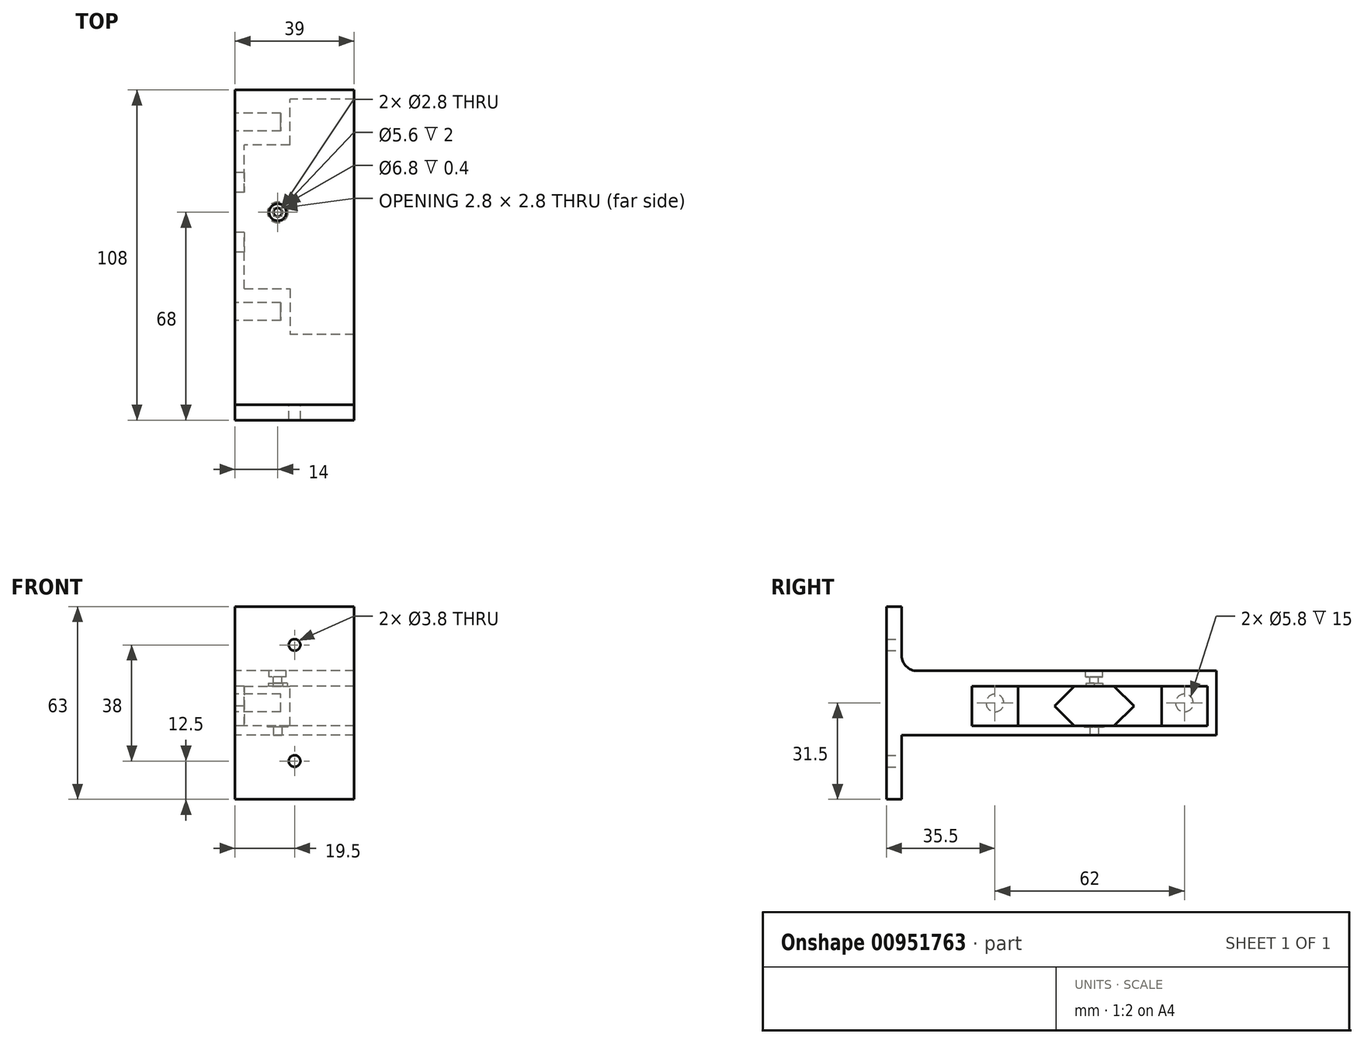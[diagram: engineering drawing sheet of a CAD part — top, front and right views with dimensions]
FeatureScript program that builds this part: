
annotation { "Feature Type Name" : "Feature", "Feature Type Description" : "" }
export const myFeature = defineFeature(function(context is Context, id is Id, definition is map)
    precondition{}
    {
        {
            var Q0;
            Q0=qCreatedBy(makeId("Top.planeOp"),FACE);
            var sketch = newSketch(context, id + "F0", { "sketchPlane" : qUnion([Q0])});
            skLineSegment(sketch, "E0", {"start": v(0, 83) * mm, "end": v(0, 0) * mm});
            skLineSegment(sketch, "E1", {"start": v(0, 0) * mm, "end": v(-39, 0) * mm});
            skLineSegment(sketch, "E2", {"start": v(-39, 0) * mm, "end": v(-39, 3) * mm});
            skLineSegment(sketch, "E3", {"start": v(-39, 3) * mm, "end": v(-3, 3) * mm});
            skLineSegment(sketch, "E4", {"start": v(-3, 3) * mm, "end": v(-3, 83) * mm});
            skLineSegment(sketch, "E5", {"start": v(-3, 83) * mm, "end": v(0, 83) * mm});
            skSolve(sketch);
        }
        {
            var Q0;
            Q0=qSketchRegion(id+"F0",true);
            extrude(context, id + "F1", {"entities" : qUnion([Q0]), "endBound" : BoundingType.SYMMETRIC, "depth" : 18 * mm, "offsetDistance" : 25 * mm});
        }
        {
            var Q0;
            Q0=makeQuery(id+"F1.opExtrude","CAP_FACE",FACE,{"disambiguationData":[OSD([sQuery(id+"F0.wireOp",EDGE,"E0"),sQuery(id+"F0.wireOp",EDGE,"E1"),sQuery(id+"F0.wireOp",EDGE,"E2"),sQuery(id+"F0.wireOp",EDGE,"E3"),sQuery(id+"F0.wireOp",EDGE,"E4"),sQuery(id+"F0.wireOp",EDGE,"E5")])],"isStart":false});
            var sketch = newSketch(context, id + "F2", { "sketchPlane" : qUnion([Q0])});
            skLineSegment(sketch, "E6.0", {"start": v(0, 83) * mm, "end": v(0, 0) * mm});
            skLineSegment(sketch, "E6.1", {"start": v(0, 0) * mm, "end": v(-39, 0) * mm});
            skLineSegment(sketch, "E7", {"start": v(-39, 0) * mm, "end": v(-39, 83) * mm});
            skLineSegment(sketch, "E8", {"start": v(-39, 83) * mm, "end": v(0, 83) * mm});
            skSolve(sketch);
        }
        {
            var Q0;
            Q0=qSketchRegion(id+"F2",true);
            extrude(context, id + "F3", {"entities" : qUnion([Q0]), "operationType" : NewBodyOperationType.ADD, "oppositeDirection" : true, "depth" : 5 * mm, "offsetDistance" : 25 * mm});
        }
        {
            var Q0;
            Q0=makeQuery(id+"F3.boolean.opBoolean","MERGE",FACE,{"derivedFrom":[makeQuery(id+"F1.opExtrude","CAP_FACE",FACE,{"disambiguationData":[OSD([sQuery(id+"F0.wireOp",EDGE,"E0"),sQuery(id+"F0.wireOp",EDGE,"E1"),sQuery(id+"F0.wireOp",EDGE,"E2"),sQuery(id+"F0.wireOp",EDGE,"E3"),sQuery(id+"F0.wireOp",EDGE,"E4"),sQuery(id+"F0.wireOp",EDGE,"E5")])],"isStart":false}),makeQuery(id+"F3.opExtrude","CAP_FACE",FACE,{"disambiguationData":[OSD([sQuery(id+"F2.wireOp",EDGE,"E6.0"),sQuery(id+"F2.wireOp",EDGE,"E6.1"),sQuery(id+"F2.wireOp",EDGE,"E7"),sQuery(id+"F2.wireOp",EDGE,"E8")])],"isStart":true})]});
            var sketch = newSketch(context, id + "F4", { "sketchPlane" : qUnion([Q0])});
            skCircle(sketch, "E9", {"center": v(-22, 60.5) * mm, "radius": 1.9 * mm});
            skCircle(sketch, "E10", {"center": v(-22, 25.5) * mm, "radius": 1.9 * mm});
            skLineSegment(sketch, "E11", {"start": v(-22, 60.5) * mm, "end": v(-22, 83) * mm});
            skLineSegment(sketch, "E12", {"start": v(-22, 25.5) * mm, "end": v(-22, 3) * mm});
            skSolve(sketch);
        }
        {
            var Q0;
            Q0=makeQuery(id+"F3.boolean.opBoolean","MERGE",FACE,{"derivedFrom":[makeQuery(id+"F1.opExtrude","SWEPT_FACE",FACE,{"disambiguationData":[OSD([sQuery(id+"F0.wireOp",EDGE,"E5")])]}),makeQuery(id+"F3.opExtrude","SWEPT_FACE",FACE,{"disambiguationData":[OSD([sQuery(id+"F2.wireOp",EDGE,"E8")])]})]});
            var sketch = newSketch(context, id + "F5", { "sketchPlane" : qUnion([Q0])});
            skLineSegment(sketch, "E13", {"start": v(0, 9) * mm, "end": v(18, 9) * mm});
            skLineSegment(sketch, "E14", {"start": v(18, 9) * mm, "end": v(18, -9) * mm});
            skLineSegment(sketch, "E15", {"start": v(18, -9) * mm, "end": v(0, -9) * mm});
            skLineSegment(sketch, "E16", {"start": v(0, -9) * mm, "end": v(0, 9) * mm});
            skSolve(sketch);
        }
        {
            var Q0;
            {var subQ5=makeQuery(id+"F1.opExtrude","SWEPT_EDGE",EDGE,{"disambiguationData":[OSD([sQuery(id+"F0.wireOp",EDGE,"E4"),sQuery(id+"F0.wireOp",EDGE,"E5")])]});Q0=makeQuery(id+"F5.imprint","IMPRINT",FACE,{"disambiguationData":[TD([[makeQuery(id+"F5.imprint","IMPRINT",EDGE,{"derivedFrom":subQ5}),1.0]])]});}
            extrude(context, id + "F6", {"entities" : qUnion([Q0]), "operationType" : NewBodyOperationType.ADD, "oppositeDirection" : true, "depth" : 18 * mm, "offsetDistance" : 25 * mm});
        }
        {
            var Q0;
            Q0=makeQuery(id+"F6.boolean.opBoolean","MERGE",FACE,{"derivedFrom":[makeQuery(id+"F1.opExtrude","CAP_FACE",FACE,{"disambiguationData":[OSD([sQuery(id+"F0.wireOp",EDGE,"E0"),sQuery(id+"F0.wireOp",EDGE,"E1"),sQuery(id+"F0.wireOp",EDGE,"E2"),sQuery(id+"F0.wireOp",EDGE,"E3"),sQuery(id+"F0.wireOp",EDGE,"E4"),sQuery(id+"F0.wireOp",EDGE,"E5")])],"isStart":true}),makeQuery(id+"F6.opExtrude","SWEPT_FACE",FACE,{"disambiguationData":[OSD([sQuery(id+"F5.wireOp",EDGE,"E15")])]})]});
            var sketch = newSketch(context, id + "F7", { "sketchPlane" : qUnion([Q0])});
            skLineSegment(sketch, "E17", {"start": v(0, 0) * mm, "end": v(-18, 0) * mm});
            skLineSegment(sketch, "E18", {"start": v(-18, 0) * mm, "end": v(-18, -18) * mm});
            skLineSegment(sketch, "E19", {"start": v(-18, -18) * mm, "end": v(0, -18) * mm});
            skLineSegment(sketch, "E20", {"start": v(0, -18) * mm, "end": v(0, 0) * mm});
            skSolve(sketch);
        }
        {
            var Q0;
            Q0=qSketchRegion(id+"F7",true);
            extrude(context, id + "F8", {"entities" : qUnion([Q0]), "operationType" : NewBodyOperationType.ADD, "oppositeDirection" : true, "depth" : 18 * mm, "offsetDistance" : 25 * mm});
        }
        {
            var Q0;
            Q0=makeQuery(id+"F8.boolean.opBoolean","MERGE",FACE,{"derivedFrom":[makeQuery(id+"F6.boolean.opBoolean","MERGE",FACE,{"derivedFrom":[makeQuery(id+"F1.opExtrude","CAP_FACE",FACE,{"disambiguationData":[OSD([sQuery(id+"F0.wireOp",EDGE,"E0"),sQuery(id+"F0.wireOp",EDGE,"E1"),sQuery(id+"F0.wireOp",EDGE,"E2"),sQuery(id+"F0.wireOp",EDGE,"E3"),sQuery(id+"F0.wireOp",EDGE,"E4"),sQuery(id+"F0.wireOp",EDGE,"E5")])],"isStart":true}),makeQuery(id+"F6.opExtrude","SWEPT_FACE",FACE,{"disambiguationData":[OSD([sQuery(id+"F5.wireOp",EDGE,"E15")])]})]}),makeQuery(id+"F8.opExtrude","CAP_FACE",FACE,{"disambiguationData":[OSD([sQuery(id+"F7.wireOp",EDGE,"E17"),sQuery(id+"F7.wireOp",EDGE,"E18"),sQuery(id+"F7.wireOp",EDGE,"E19"),sQuery(id+"F7.wireOp",EDGE,"E20")])],"isStart":true})]});
            var sketch = newSketch(context, id + "F9", { "sketchPlane" : qUnion([Q0])});
            skLineSegment(sketch, "E21.0.0", {"start": v(0, -83) * mm, "end": v(-22, -83) * mm});
            skLineSegment(sketch, "E21.0.1", {"start": v(-22, -83) * mm, "end": v(-39, -83) * mm});
            skLineSegment(sketch, "E21.0.2", {"start": v(-39, -83) * mm, "end": v(-39, 0) * mm});
            skLineSegment(sketch, "E21.0.3", {"start": v(-39, 0) * mm, "end": v(0, 0) * mm});
            skLineSegment(sketch, "E21.0.4", {"start": v(0, 0) * mm, "end": v(0, -83) * mm});
            skSolve(sketch);
        }
        {
            var Q0;
            Q0=qSketchRegion(id+"F9",true);
            extrude(context, id + "F10", {"entities" : qUnion([Q0]), "operationType" : NewBodyOperationType.ADD, "depth" : 3 * mm, "offsetDistance" : 25 * mm});
        }
        {
            var Q0;
            Q0=makeQuery(id+"F4.imprint","IMPRINT",FACE,{"disambiguationData":[TD([[makeQuery(id+"F4.imprint","IMPRINT",EDGE,{"derivedFrom":sQuery(id+"F4.wireOp",EDGE,"E9")}),-1.0]])]});
            var sketch = newSketch(context, id + "F11", { "sketchPlane" : qUnion([Q0])});
            skCircle(sketch, "E22", {"center": v(-14, 43) * mm, "radius": 17.34 * mm});
            skCircle(sketch, "E23", {"center": v(-14, 43) * mm, "radius": 14.84 * mm});
            skSolve(sketch);
        }
        {
            var Q0;
            Q0=makeQuery(id+"F10.boolean.opBoolean","MERGE",FACE,{"derivedFrom":[makeQuery(id+"F1.opExtrude","SWEPT_FACE",FACE,{"disambiguationData":[OSD([sQuery(id+"F0.wireOp",EDGE,"E0")])]}),makeQuery(id+"F10.opExtrude","SWEPT_FACE",FACE,{"disambiguationData":[OSD([sQuery(id+"F9.wireOp",EDGE,"E21.0.4")])]})]});
            var sketch = newSketch(context, id + "F12", { "sketchPlane" : qUnion([Q0])});
            skLineSegment(sketch, "E24.top", {"start": v(36.5, -9) * mm, "end": v(49.5, -9) * mm});
            skLineSegment(sketch, "E24.left", {"start": v(36.5, 4) * mm, "end": v(36.5, -9) * mm});
            skLineSegment(sketch, "E24.right", {"start": v(49.5, 4) * mm, "end": v(49.5, -9) * mm});
            skLineSegment(sketch, "E25", {"start": v(36.5, 4) * mm, "end": v(30, -2.5) * mm});
            skPoint(sketch, "E25.endSnap0", {"position": v(36.5, -2.5) * mm});
            skLineSegment(sketch, "E26", {"start": v(30, -2.5) * mm, "end": v(36.5, -9) * mm});
            skLineSegment(sketch, "E27", {"start": v(49.5, 4) * mm, "end": v(56, -2.5) * mm});
            skLineSegment(sketch, "E28", {"start": v(56, -2.5) * mm, "end": v(49.5, -9) * mm});
            skCircle(sketch, "E29", {"center": v(10.5, -1.5) * mm, "radius": 2.9 * mm});
            skCircle(sketch, "E30", {"center": v(72.5, -1.5) * mm, "radius": 2.9 * mm});
            skLineSegment(sketch, "E31", {"start": v(0, -1.5) * mm, "end": v(10.5, -1.5) * mm});
            skLineSegment(sketch, "E32", {"start": v(72.5, -1.5) * mm, "end": v(83, -1.5) * mm});
            skLineSegment(sketch, "E33", {"start": v(10.5, -1.5) * mm, "end": v(10.5, -12) * mm});
            skLineSegment(sketch, "E34", {"start": v(49.5, 4) * mm, "end": v(36.5, 4) * mm});
            skSolve(sketch);
        }
        {
            var Q0;
            {var subQ0=sQuery(id+"F12.wireOp",EDGE,"E31");var subQ1=sQuery(id+"F12.wireOp",EDGE,"E29");var subQ2=makeQuery(id+"F12.imprint","INTERSECT",VERTEX,{"derivedFrom":[subQ1,subQ0]});Q0=makeQuery(id+"F12.imprint","IMPRINT",FACE,{"disambiguationData":[TD([[makeQuery(id+"F12.imprint","IMPRINT",EDGE,{"disambiguationData":[TD([[subQ2,-1.0]])],"derivedFrom":subQ1}),1.0]])]});}
            var Q1;
            {var subQ0=sQuery(id+"F12.wireOp",EDGE,"E31");var subQ1=sQuery(id+"F12.wireOp",EDGE,"E29");var subQ2=makeQuery(id+"F12.imprint","INTERSECT",VERTEX,{"derivedFrom":[subQ1,subQ0]});Q1=makeQuery(id+"F12.imprint","IMPRINT",FACE,{"disambiguationData":[TD([[makeQuery(id+"F12.imprint","IMPRINT",EDGE,{"disambiguationData":[TD([[subQ2,1.0]])],"derivedFrom":subQ1}),1.0]])]});}
            var Q2;
            Q2=makeQuery(id+"F12.imprint","IMPRINT",FACE,{"disambiguationData":[TD([[makeQuery(id+"F12.imprint","IMPRINT",EDGE,{"derivedFrom":sQuery(id+"F12.wireOp",EDGE,"E24.left")}),-1.0]])]});
            var Q3;
            Q3=makeQuery(id+"F12.imprint","IMPRINT",FACE,{"disambiguationData":[TD([[makeQuery(id+"F12.imprint","IMPRINT",EDGE,{"derivedFrom":sQuery(id+"F12.wireOp",EDGE,"E24.top")}),1.0]])]});
            var Q4;
            Q4=makeQuery(id+"F12.imprint","IMPRINT",FACE,{"disambiguationData":[TD([[makeQuery(id+"F12.imprint","IMPRINT",EDGE,{"derivedFrom":sQuery(id+"F12.wireOp",EDGE,"E24.right")}),1.0]])]});
            var Q5;
            Q5=makeQuery(id+"F12.imprint","IMPRINT",FACE,{"disambiguationData":[TD([[makeQuery(id+"F12.imprint","IMPRINT",EDGE,{"derivedFrom":sQuery(id+"F12.wireOp",EDGE,"E30")}),1.0]])]});
            extrude(context, id + "F13", {"entities" : qUnion([Q0, Q1, Q2, Q3, Q4, Q5]), "operationType" : NewBodyOperationType.REMOVE, "oppositeDirection" : true, "depth" : 15 * mm, "offsetDistance" : 25 * mm});
        }
        {
            var Q0;
            Q0=makeQuery(id+"F6.opExtrude","SWEPT_FACE",FACE,{"disambiguationData":[OSD([sQuery(id+"F5.wireOp",EDGE,"E14")])]});
            var sketch = newSketch(context, id + "F14", { "sketchPlane" : qUnion([Q0])});
            skLineSegment(sketch, "E35", {"start": v(-83, 4) * mm, "end": v(-80, 4) * mm});
            skLineSegment(sketch, "E36", {"start": v(-80, 4) * mm, "end": v(-80, -9) * mm});
            skLineSegment(sketch, "E37", {"start": v(-80, -9) * mm, "end": v(-83, -9) * mm});
            skLineSegment(sketch, "E38", {"start": v(-83, -9) * mm, "end": v(-83, 4) * mm});
            skSolve(sketch);
        }
        {
            var Q0;
            Q0=makeQuery(id+"F14.imprint","IMPRINT",FACE,{"disambiguationData":[TD([[makeQuery(id+"F14.imprint","IMPRINT",EDGE,{"derivedFrom":sQuery(id+"F14.wireOp",EDGE,"E35")}),1.0]])]});
            var Q1;
            Q1=makeQuery(id+"F10.boolean.opBoolean","MERGE",FACE,{"derivedFrom":[makeQuery(id+"F3.boolean.opBoolean","MERGE",FACE,{"derivedFrom":[makeQuery(id+"F1.opExtrude","SWEPT_FACE",FACE,{"disambiguationData":[OSD([sQuery(id+"F0.wireOp",EDGE,"E2")])]}),makeQuery(id+"F3.opExtrude","SWEPT_FACE",FACE,{"disambiguationData":[OSD([sQuery(id+"F2.wireOp",EDGE,"E7")])]})]}),makeQuery(id+"F10.opExtrude","SWEPT_FACE",FACE,{"disambiguationData":[OSD([sQuery(id+"F9.wireOp",EDGE,"E21.0.2")])]})]});
            extrude(context, id + "F15", {"entities" : qUnion([Q0]), "operationType" : NewBodyOperationType.ADD, "endBound" : BoundingType.UP_TO_SURFACE, "depth" : 25 * mm, "endBoundEntityFace" : qUnion([Q1]), "offsetDistance" : 25 * mm});
        }
        {
            var Q0;
            Q0=makeQuery(id+"F10.boolean.opBoolean","MERGE",FACE,{"derivedFrom":[makeQuery(id+"F1.opExtrude","SWEPT_FACE",FACE,{"disambiguationData":[OSD([sQuery(id+"F0.wireOp",EDGE,"E1")])]}),makeQuery(id+"F10.opExtrude","SWEPT_FACE",FACE,{"disambiguationData":[OSD([sQuery(id+"F9.wireOp",EDGE,"E21.0.3")])]})]});
            var sketch = newSketch(context, id + "F16", { "sketchPlane" : qUnion([Q0])});
            skLineSegment(sketch, "E39.0", {"start": v(0, -12) * mm, "end": v(-39, -12) * mm});
            skLineSegment(sketch, "E39.1", {"start": v(0, 9) * mm, "end": v(0, -12) * mm});
            skLineSegment(sketch, "E39.2", {"start": v(0, 9) * mm, "end": v(-39, 9) * mm});
            skLineSegment(sketch, "E39.3", {"start": v(-39, 9) * mm, "end": v(-39, -12) * mm});
            skSolve(sketch);
        }
        {
            var Q0;
            Q0=makeQuery(id+"F16.imprint","IMPRINT",FACE,{"disambiguationData":[TD([[makeQuery(id+"F16.imprint","IMPRINT",EDGE,{"derivedFrom":sQuery(id+"F16.wireOp",EDGE,"E39.0")}),-1.0]])]});
            extrude(context, id + "F17", {"entities" : qUnion([Q0]), "operationType" : NewBodyOperationType.ADD, "depth" : 20 * mm, "offsetDistance" : 25 * mm});
        }
        {
            var Q0;
            Q0=makeQuery(id+"F17.opExtrude","CAP_FACE",FACE,{"disambiguationData":[OSD([sQuery(id+"F16.wireOp",EDGE,"E39.0"),sQuery(id+"F16.wireOp",EDGE,"E39.1"),sQuery(id+"F16.wireOp",EDGE,"E39.2"),sQuery(id+"F16.wireOp",EDGE,"E39.3")])],"isStart":false});
            var sketch = newSketch(context, id + "F18", { "sketchPlane" : qUnion([Q0])});
            skLineSegment(sketch, "E40", {"start": v(-39, 30) * mm, "end": v(-39, 9) * mm});
            skLineSegment(sketch, "E41", {"start": v(-39, 9) * mm, "end": v(-39, -12) * mm});
            skLineSegment(sketch, "E42", {"start": v(-39, -12) * mm, "end": v(-39, -33) * mm});
            skLineSegment(sketch, "E43", {"start": v(-39, -33) * mm, "end": v(0, -33) * mm});
            skLineSegment(sketch, "E44", {"start": v(0, -33) * mm, "end": v(0, -12) * mm});
            skLineSegment(sketch, "E45", {"start": v(0, -12) * mm, "end": v(0, 9) * mm});
            skLineSegment(sketch, "E46", {"start": v(0, 9) * mm, "end": v(0, 30) * mm});
            skLineSegment(sketch, "E47", {"start": v(0, 30) * mm, "end": v(-39, 30) * mm});
            skSolve(sketch);
        }
        {
            var Q0;
            Q0=qSketchRegion(id+"F18",true);
            extrude(context, id + "F19", {"entities" : qUnion([Q0]), "operationType" : NewBodyOperationType.ADD, "depth" : 3 * mm, "offsetDistance" : 25 * mm});
        }
        {
            var Q0;
            Q0=makeQuery(id+"F17.opExtrude","CAP_EDGE",EDGE,{"disambiguationData":[OSD([sQuery(id+"F16.wireOp",EDGE,"E39.0")])],"isStart":false});
            var Q1;
            Q1=makeQuery(id+"F17.opExtrude","CAP_EDGE",EDGE,{"disambiguationData":[OSD([sQuery(id+"F16.wireOp",EDGE,"E39.2")])],"isStart":false});
            fillet(context, id + "F20", {"entities" : qUnion([Q0, Q1]), "radius" : 5 * mm, "tangentPropagation" : true, "allowEdgeOverflow" : false});
        }
        {
            var Q0;
            Q0=makeQuery(id+"F19.opExtrude","CAP_FACE",FACE,{"disambiguationData":[OSD([sQuery(id+"F18.wireOp",EDGE,"E40"),sQuery(id+"F18.wireOp",EDGE,"E41"),sQuery(id+"F18.wireOp",EDGE,"E42"),sQuery(id+"F18.wireOp",EDGE,"E43"),sQuery(id+"F18.wireOp",EDGE,"E44"),sQuery(id+"F18.wireOp",EDGE,"E45"),sQuery(id+"F18.wireOp",EDGE,"E46"),sQuery(id+"F18.wireOp",EDGE,"E47")])],"isStart":false});
            var sketch = newSketch(context, id + "F21", { "sketchPlane" : qUnion([Q0])});
            skLineSegment(sketch, "E48.bottom", {"start": v(-32, 23) * mm, "end": v(-7, 23) * mm});
            skLineSegment(sketch, "E48.top", {"start": v(-32, -26) * mm, "end": v(-7, -26) * mm});
            skLineSegment(sketch, "E48.left", {"start": v(-32, 23) * mm, "end": v(-32, -26) * mm});
            skLineSegment(sketch, "E48.right", {"start": v(-7, 23) * mm, "end": v(-7, -26) * mm});
            skCircle(sketch, "E49", {"center": v(-32, -26) * mm, "radius": 1.9 * mm});
            skCircle(sketch, "E50", {"center": v(-7, -26) * mm, "radius": 1.9 * mm});
            skCircle(sketch, "E51", {"center": v(-7, 23) * mm, "radius": 1.9 * mm});
            skCircle(sketch, "E52", {"center": v(-32, 23) * mm, "radius": 1.9 * mm});
            skSolve(sketch);
        }
        {
            var Q0;
            {var subQ0=sQuery(id+"F21.wireOp",EDGE,"E48.left");var subQ1=sQuery(id+"F21.wireOp",EDGE,"E48.bottom");var subQ2=makeQuery(id+"F21.imprint","INTERSECT",VERTEX,{"derivedFrom":[subQ1,subQ0]});Q0=makeQuery(id+"F21.imprint","IMPRINT",FACE,{"disambiguationData":[TD([[makeQuery(id+"F21.imprint","IMPRINT",EDGE,{"disambiguationData":[TD([[subQ2,-1.0]])],"derivedFrom":subQ1}),1.0]])]});}
            var Q1;
            {var subQ0=sQuery(id+"F21.wireOp",EDGE,"E48.left");var subQ1=sQuery(id+"F21.wireOp",EDGE,"E48.bottom");var subQ2=makeQuery(id+"F21.imprint","INTERSECT",VERTEX,{"derivedFrom":[subQ1,subQ0]});Q1=makeQuery(id+"F21.imprint","IMPRINT",FACE,{"disambiguationData":[TD([[makeQuery(id+"F21.imprint","IMPRINT",EDGE,{"disambiguationData":[TD([[subQ2,-1.0]])],"derivedFrom":subQ1}),-1.0]])]});}
            var Q2;
            {var subQ0=sQuery(id+"F21.wireOp",EDGE,"E48.right");var subQ1=sQuery(id+"F21.wireOp",EDGE,"E48.bottom");var subQ2=makeQuery(id+"F21.imprint","INTERSECT",VERTEX,{"derivedFrom":[subQ1,subQ0]});Q2=makeQuery(id+"F21.imprint","IMPRINT",FACE,{"disambiguationData":[TD([[makeQuery(id+"F21.imprint","IMPRINT",EDGE,{"disambiguationData":[TD([[subQ2,1.0]])],"derivedFrom":subQ1}),1.0]])]});}
            var Q3;
            {var subQ0=sQuery(id+"F21.wireOp",EDGE,"E48.right");var subQ1=sQuery(id+"F21.wireOp",EDGE,"E48.bottom");var subQ2=makeQuery(id+"F21.imprint","INTERSECT",VERTEX,{"derivedFrom":[subQ1,subQ0]});Q3=makeQuery(id+"F21.imprint","IMPRINT",FACE,{"disambiguationData":[TD([[makeQuery(id+"F21.imprint","IMPRINT",EDGE,{"disambiguationData":[TD([[subQ2,1.0]])],"derivedFrom":subQ1}),-1.0]])]});}
            var Q4;
            {var subQ0=sQuery(id+"F21.wireOp",EDGE,"E48.left");var subQ1=sQuery(id+"F21.wireOp",EDGE,"E48.top");var subQ2=makeQuery(id+"F21.imprint","INTERSECT",VERTEX,{"derivedFrom":[subQ1,subQ0]});Q4=makeQuery(id+"F21.imprint","IMPRINT",FACE,{"disambiguationData":[TD([[makeQuery(id+"F21.imprint","IMPRINT",EDGE,{"disambiguationData":[TD([[subQ2,-1.0]])],"derivedFrom":subQ1}),-1.0]])]});}
            var Q5;
            {var subQ0=sQuery(id+"F21.wireOp",EDGE,"E48.left");var subQ1=sQuery(id+"F21.wireOp",EDGE,"E48.top");var subQ2=makeQuery(id+"F21.imprint","INTERSECT",VERTEX,{"derivedFrom":[subQ1,subQ0]});Q5=makeQuery(id+"F21.imprint","IMPRINT",FACE,{"disambiguationData":[TD([[makeQuery(id+"F21.imprint","IMPRINT",EDGE,{"disambiguationData":[TD([[subQ2,-1.0]])],"derivedFrom":subQ1}),1.0]])]});}
            var Q6;
            {var subQ0=sQuery(id+"F21.wireOp",EDGE,"E48.right");var subQ1=sQuery(id+"F21.wireOp",EDGE,"E48.top");var subQ2=makeQuery(id+"F21.imprint","INTERSECT",VERTEX,{"derivedFrom":[subQ1,subQ0]});Q6=makeQuery(id+"F21.imprint","IMPRINT",FACE,{"disambiguationData":[TD([[makeQuery(id+"F21.imprint","IMPRINT",EDGE,{"disambiguationData":[TD([[subQ2,1.0]])],"derivedFrom":subQ1}),-1.0]])]});}
            var Q7;
            {var subQ0=sQuery(id+"F21.wireOp",EDGE,"E48.right");var subQ1=sQuery(id+"F21.wireOp",EDGE,"E48.top");var subQ2=makeQuery(id+"F21.imprint","INTERSECT",VERTEX,{"derivedFrom":[subQ1,subQ0]});Q7=makeQuery(id+"F21.imprint","IMPRINT",FACE,{"disambiguationData":[TD([[makeQuery(id+"F21.imprint","IMPRINT",EDGE,{"disambiguationData":[TD([[subQ2,1.0]])],"derivedFrom":subQ1}),1.0]])]});}
            extrude(context, id + "F22", {"entities" : qUnion([Q0, Q1, Q2, Q3, Q4, Q5, Q6, Q7]), "operationType" : NewBodyOperationType.REMOVE, "oppositeDirection" : true, "depth" : 25 * mm, "offsetDistance" : 25 * mm});
        }
        {
            var Q0;
            {var subQ0=sQuery(id+"F11.wireOp",EDGE,"E23");var subQ1=makeQuery(id+"F4.imprint","IMPRINT",EDGE,{"derivedFrom":makeQuery(id+"F1.opExtrude","CAP_EDGE",EDGE,{"disambiguationData":[OSD([sQuery(id+"F0.wireOp",EDGE,"E0")])],"isStart":false})});var subQ2=makeQuery(id+"F11.imprint","INTERSECT",VERTEX,{"disambiguationData":[OD(0.0)],"derivedFrom":[subQ1,subQ0]});Q0=makeQuery(id+"F11.imprint","IMPRINT",FACE,{"disambiguationData":[TD([[makeQuery(id+"F11.imprint","IMPRINT",EDGE,{"disambiguationData":[TD([[subQ2,-1.0]])],"derivedFrom":subQ0}),1.0]])]});}
            var sketch = newSketch(context, id + "F23", { "sketchPlane" : qUnion([Q0])});
            skCircle(sketch, "E53", {"center": v(-14, 43) * mm, "radius": 2.4 * mm});
            skSolve(sketch);
        }
        {
            var Q0;
            Q0=makeQuery(id+"F23.imprint","IMPRINT",FACE,{"disambiguationData":[TD([[makeQuery(id+"F23.imprint","IMPRINT",EDGE,{"derivedFrom":sQuery(id+"F23.wireOp",EDGE,"E53")}),1.0]])]});
            extrude(context, id + "F24", {"entities" : qUnion([Q0]), "operationType" : NewBodyOperationType.REMOVE, "oppositeDirection" : true, "depth" : 25 * mm, "offsetDistance" : 25 * mm});
        }
        {
            var Q0;
            {var subQ11=makeQuery(id+"F4.imprint","IMPRINT",EDGE,{"derivedFrom":makeQuery(id+"F1.opExtrude","CAP_EDGE",EDGE,{"disambiguationData":[OSD([sQuery(id+"F0.wireOp",EDGE,"E1")])],"isStart":false})});Q0=makeQuery(id+"F11.imprint","IMPRINT",FACE,{"disambiguationData":[TD([[makeQuery(id+"F11.imprint","IMPRINT",EDGE,{"derivedFrom":subQ11}),-1.0]])]});}
            var sketch = newSketch(context, id + "F25", { "sketchPlane" : qUnion([Q0])});
            skCircle(sketch, "E54.cCircle", {"center": v(-14, 43) * mm, "radius": 4.73 * mm, "construction": true});
            skLineSegment(sketch, "E54.0", {"start": v(-11.63, 47.1) * mm, "end": v(-9.27, 43) * mm});
            skLineSegment(sketch, "E54.1", {"start": v(-9.27, 43) * mm, "end": v(-11.63, 38.9) * mm});
            skLineSegment(sketch, "E54.2", {"start": v(-11.63, 38.9) * mm, "end": v(-16.37, 38.9) * mm});
            skLineSegment(sketch, "E54.3", {"start": v(-16.37, 38.9) * mm, "end": v(-18.73, 43) * mm});
            skLineSegment(sketch, "E54.4", {"start": v(-18.73, 43) * mm, "end": v(-16.37, 47.1) * mm});
            skLineSegment(sketch, "E54.5", {"start": v(-16.37, 47.1) * mm, "end": v(-11.63, 47.1) * mm});
            skSolve(sketch);
        }
        {
            var Q0;
            Q0=makeQuery(id+"F25.imprint","IMPRINT",FACE,{"disambiguationData":[TD([[makeQuery(id+"F25.imprint","IMPRINT",EDGE,{"derivedFrom":sQuery(id+"F25.wireOp",EDGE,"E54.0")}),-1.0]])]});
            extrude(context, id + "F26", {"entities" : qUnion([Q0]), "operationType" : NewBodyOperationType.REMOVE, "oppositeDirection" : true, "depth" : 2.5 * mm, "offsetDistance" : 25 * mm});
        }
        {
            var Q0;
            Q0=qCreatedBy(makeId("Right.planeOp"),FACE);
            cPlane(context, id + "F27", {"entities" : qUnion([Q0]), "cplaneType" : CPlaneType.OFFSET, "offset" : 25 * mm, "width" : 150 * mm, "height" : 150 * mm});
        }
        {
            var Q0;
            Q0=makeQuery(id+"F1.opExtrude","SWEPT_BODY",BODY,{"disambiguationData":[OSD([sQuery(id+"F0.wireOp",EDGE,"E0"),sQuery(id+"F0.wireOp",EDGE,"E1"),sQuery(id+"F0.wireOp",EDGE,"E2"),sQuery(id+"F0.wireOp",EDGE,"E3"),sQuery(id+"F0.wireOp",EDGE,"E4"),sQuery(id+"F0.wireOp",EDGE,"E5")])]});
            var Q1;
            Q1=qCreatedBy(id+"F27.planeOp",FACE);
            mirror(context, id + "F28", {"entities" : qUnion([Q0]), "mirrorPlane" : qUnion([Q1])});
        }
        {
            var Q0;
            Q0=makeQuery(id+"F28.opPattern","COPY",BODY,{"derivedFrom":makeQuery(id+"F1.opExtrude","SWEPT_BODY",BODY,{"disambiguationData":[OSD([sQuery(id+"F0.wireOp",EDGE,"E0"),sQuery(id+"F0.wireOp",EDGE,"E1"),sQuery(id+"F0.wireOp",EDGE,"E2"),sQuery(id+"F0.wireOp",EDGE,"E3"),sQuery(id+"F0.wireOp",EDGE,"E4"),sQuery(id+"F0.wireOp",EDGE,"E5")])]}),"instanceName":"1"});
            var Q1;
            Q1=qCreatedBy(id+"F27.planeOp",FACE);
            mirror(context, id + "F29", {"operationType" : NewBodyOperationType.REMOVE, "entities" : qUnion([Q0]), "mirrorPlane" : qUnion([Q1])});
        }
        {
            var Q0;
            {var subQ0=sQuery(id+"F18.wireOp",EDGE,"E46");var subQ1=sQuery(id+"F18.wireOp",EDGE,"E45");var subQ2=sQuery(id+"F18.wireOp",EDGE,"E44");var subQ6=sQuery(id+"F18.wireOp",EDGE,"E42");var subQ7=sQuery(id+"F18.wireOp",EDGE,"E41");var subQ8=sQuery(id+"F18.wireOp",EDGE,"E40");var subQ9=sQuery(id+"F18.wireOp",EDGE,"E47");Q0=makeQuery(id+"F28.opPattern","COPY",FACE,{"derivedFrom":makeQuery(id+"F19.boolean.opBoolean","SPLIT",FACE,{"disambiguationData":[TD([makeQuery(id+"F17.opExtrude","SWEPT_FACE",FACE,{"disambiguationData":[OSD([sQuery(id+"F16.wireOp",EDGE,"E39.2")])]})])],"derivedFrom":makeQuery(id+"F19.opExtrude","CAP_FACE",FACE,{"disambiguationData":[OSD([subQ8,subQ7,subQ6,sQuery(id+"F18.wireOp",EDGE,"E43"),subQ2,subQ1,subQ0,subQ9])],"isStart":true})}),"instanceName":"1"});}
            var sketch = newSketch(context, id + "F30", { "sketchPlane" : qUnion([Q0])});
            skCircle(sketch, "E55", {"center": v(-57.1, 22.38) * mm, "radius": 4.94 * mm});
            skCircle(sketch, "E56", {"center": v(-82, 23) * mm, "radius": 3.92 * mm});
            skCircle(sketch, "E57", {"center": v(-56.98, -25.74) * mm, "radius": 2.63 * mm});
            skCircle(sketch, "E58", {"center": v(-82.6, -26.07) * mm, "radius": 3.77 * mm});
            skSolve(sketch);
        }
        {
            var Q0;
            Q0 = qSketchRegion(id + "F30", true);
            var Q1;
            Q1=makeQuery(id+"F28.opPattern","COPY",FACE,{"derivedFrom":makeQuery(id+"F19.opExtrude","CAP_FACE",FACE,{"disambiguationData":[OSD([sQuery(id+"F18.wireOp",EDGE,"E40"),sQuery(id+"F18.wireOp",EDGE,"E41"),sQuery(id+"F18.wireOp",EDGE,"E42"),sQuery(id+"F18.wireOp",EDGE,"E43"),sQuery(id+"F18.wireOp",EDGE,"E44"),sQuery(id+"F18.wireOp",EDGE,"E45"),sQuery(id+"F18.wireOp",EDGE,"E46"),sQuery(id+"F18.wireOp",EDGE,"E47")])],"isStart":false}),"instanceName":"1"});
            extrude(context, id + "F31", {"entities" : qUnion([Q0]), "operationType" : NewBodyOperationType.ADD, "endBound" : BoundingType.UP_TO_SURFACE, "oppositeDirection" : true, "depth" : 25 * mm, "endBoundEntityFace" : qUnion([Q1]), "offsetDistance" : 25 * mm});
        }
        {
            var Q0;
            {var subQ0=sQuery(id+"F18.wireOp",EDGE,"E46");var subQ1=sQuery(id+"F18.wireOp",EDGE,"E45");var subQ2=sQuery(id+"F18.wireOp",EDGE,"E44");var subQ6=sQuery(id+"F18.wireOp",EDGE,"E42");var subQ7=sQuery(id+"F18.wireOp",EDGE,"E41");var subQ8=sQuery(id+"F18.wireOp",EDGE,"E40");var subQ9=sQuery(id+"F18.wireOp",EDGE,"E47");Q0=makeQuery(id+"F31.boolean.opBoolean","MERGE",FACE,{"derivedFrom":[makeQuery(id+"F28.opPattern","COPY",FACE,{"derivedFrom":makeQuery(id+"F19.boolean.opBoolean","SPLIT",FACE,{"disambiguationData":[TD([makeQuery(id+"F17.opExtrude","SWEPT_FACE",FACE,{"disambiguationData":[OSD([sQuery(id+"F16.wireOp",EDGE,"E39.2")])]})])],"derivedFrom":makeQuery(id+"F19.opExtrude","CAP_FACE",FACE,{"disambiguationData":[OSD([subQ8,subQ7,subQ6,sQuery(id+"F18.wireOp",EDGE,"E43"),subQ2,subQ1,subQ0,subQ9])],"isStart":true})}),"instanceName":"1"}),makeQuery(id+"F31.opExtrude","CAP_FACE",FACE,{"disambiguationData":[OSD([sQuery(id+"F30.wireOp",EDGE,"E55")])],"isStart":true}),makeQuery(id+"F31.opExtrude","CAP_FACE",FACE,{"disambiguationData":[OSD([sQuery(id+"F30.wireOp",EDGE,"E56")])],"isStart":true})]});}
            var sketch = newSketch(context, id + "F32", { "sketchPlane" : qUnion([Q0])});
            skCircle(sketch, "E59", {"center": v(-69.5, 17.5) * mm, "radius": 1.9 * mm});
            skCircle(sketch, "E60", {"center": v(-69.5, -20.5) * mm, "radius": 1.9 * mm});
            skLineSegment(sketch, "E61", {"start": v(-69.5, 17.5) * mm, "end": v(-69.5, -20.5) * mm});
            skLineSegment(sketch, "E62", {"start": v(-69.5, 17.5) * mm, "end": v(-69.5, 30) * mm});
            skLineSegment(sketch, "E63", {"start": v(-69.5, -20.5) * mm, "end": v(-69.5, -33) * mm});
            skSolve(sketch);
        }
        {
            var Q0;
            Q0 = qSketchRegion(id + "F32", true);
            extrude(context, id + "F33", {"entities" : qUnion([Q0]), "operationType" : NewBodyOperationType.REMOVE, "oppositeDirection" : true, "depth" : 25 * mm, "offsetDistance" : 25 * mm});
        }
        {
            var Q0;
            Q0=makeQuery(id+"F28.opPattern","COPY",FACE,{"derivedFrom":makeQuery(id+"F17.boolean.opBoolean","MERGE",FACE,{"derivedFrom":[makeQuery(id+"F3.boolean.opBoolean","MERGE",FACE,{"derivedFrom":[makeQuery(id+"F1.opExtrude","CAP_FACE",FACE,{"disambiguationData":[OSD([sQuery(id+"F0.wireOp",EDGE,"E0"),sQuery(id+"F0.wireOp",EDGE,"E1"),sQuery(id+"F0.wireOp",EDGE,"E2"),sQuery(id+"F0.wireOp",EDGE,"E3"),sQuery(id+"F0.wireOp",EDGE,"E4"),sQuery(id+"F0.wireOp",EDGE,"E5")])],"isStart":false}),makeQuery(id+"F3.opExtrude","CAP_FACE",FACE,{"disambiguationData":[OSD([sQuery(id+"F2.wireOp",EDGE,"E6.0"),sQuery(id+"F2.wireOp",EDGE,"E6.1"),sQuery(id+"F2.wireOp",EDGE,"E7"),sQuery(id+"F2.wireOp",EDGE,"E8")])],"isStart":true})]}),makeQuery(id+"F17.opExtrude","SWEPT_FACE",FACE,{"disambiguationData":[OSD([sQuery(id+"F16.wireOp",EDGE,"E39.2")])]})]}),"instanceName":"1"});
            var sketch = newSketch(context, id + "F34", { "sketchPlane" : qUnion([Q0])});
            skCircle(sketch, "E64", {"center": v(64, 43) * mm, "radius": 1.4 * mm});
            skCircle(sketch, "E65", {"center": v(64, 43) * mm, "radius": 5.83 * mm});
            skSolve(sketch);
        }
        {
            var Q0;
            Q0 = qSketchRegion(id + "F34", true);
            var Q1;
            Q1=makeQuery(id+"F28.opPattern","COPY",FACE,{"derivedFrom":makeQuery(id+"F13.boolean.opBoolean","MERGE",FACE,{"derivedFrom":[makeQuery(id+"F3.opExtrude","CAP_FACE",FACE,{"disambiguationData":[OSD([sQuery(id+"F2.wireOp",EDGE,"E6.0"),sQuery(id+"F2.wireOp",EDGE,"E6.1"),sQuery(id+"F2.wireOp",EDGE,"E7"),sQuery(id+"F2.wireOp",EDGE,"E8")])],"isStart":false})],"fromTools":[makeQuery(id+"F13.opExtrude","SWEPT_FACE",FACE,{"disambiguationData":[OSD([sQuery(id+"F12.wireOp",EDGE,"E34")])]})]}),"instanceName":"1"});
            extrude(context, id + "F35", {"entities" : qUnion([Q0]), "operationType" : NewBodyOperationType.ADD, "endBound" : BoundingType.UP_TO_SURFACE, "oppositeDirection" : true, "depth" : 25 * mm, "endBoundEntityFace" : qUnion([Q1]), "offsetDistance" : 25 * mm});
        }
        {
            var Q0;
            Q0=makeQuery(id+"F28.opPattern","COPY",FACE,{"derivedFrom":makeQuery(id+"F17.boolean.opBoolean","MERGE",FACE,{"derivedFrom":[makeQuery(id+"F10.opExtrude","CAP_FACE",FACE,{"disambiguationData":[OSD([sQuery(id+"F9.wireOp",EDGE,"E21.0.0"),sQuery(id+"F9.wireOp",EDGE,"E21.0.1"),sQuery(id+"F9.wireOp",EDGE,"E21.0.2"),sQuery(id+"F9.wireOp",EDGE,"E21.0.3"),sQuery(id+"F9.wireOp",EDGE,"E21.0.4")])],"isStart":false}),makeQuery(id+"F17.opExtrude","SWEPT_FACE",FACE,{"disambiguationData":[OSD([sQuery(id+"F16.wireOp",EDGE,"E39.0")])]})]}),"instanceName":"1"});
            var sketch = newSketch(context, id + "F36", { "sketchPlane" : qUnion([Q0])});
            skCircle(sketch, "E66", {"center": v(64, -43) * mm, "radius": 1.4 * mm});
            skCircle(sketch, "E67", {"center": v(64, -43) * mm, "radius": 4.7 * mm});
            skSolve(sketch);
        }
        {
            var Q0;
            Q0 = qSketchRegion(id + "F36", true);
            var Q1;
            Q1=makeQuery(id+"F28.opPattern","COPY",FACE,{"derivedFrom":makeQuery(id+"F13.boolean.opBoolean","MERGE",FACE,{"derivedFrom":[makeQuery(id+"F10.opExtrude","CAP_FACE",FACE,{"disambiguationData":[OSD([sQuery(id+"F9.wireOp",EDGE,"E21.0.0"),sQuery(id+"F9.wireOp",EDGE,"E21.0.1"),sQuery(id+"F9.wireOp",EDGE,"E21.0.2"),sQuery(id+"F9.wireOp",EDGE,"E21.0.3"),sQuery(id+"F9.wireOp",EDGE,"E21.0.4")])],"isStart":true})],"fromTools":[makeQuery(id+"F13.opExtrude","SWEPT_FACE",FACE,{"disambiguationData":[OSD([sQuery(id+"F12.wireOp",EDGE,"E24.top")])]})]}),"instanceName":"1"});
            extrude(context, id + "F37", {"entities" : qUnion([Q0]), "operationType" : NewBodyOperationType.ADD, "endBound" : BoundingType.UP_TO_SURFACE, "oppositeDirection" : true, "depth" : 25 * mm, "endBoundEntityFace" : qUnion([Q1]), "offsetDistance" : 25 * mm});
        }
        {
            var Q0;
            Q0=makeQuery(id+"F35.boolean.opBoolean","MERGE",FACE,{"derivedFrom":[makeQuery(id+"F28.opPattern","COPY",FACE,{"derivedFrom":makeQuery(id+"F17.boolean.opBoolean","MERGE",FACE,{"derivedFrom":[makeQuery(id+"F3.boolean.opBoolean","MERGE",FACE,{"derivedFrom":[makeQuery(id+"F1.opExtrude","CAP_FACE",FACE,{"disambiguationData":[OSD([sQuery(id+"F0.wireOp",EDGE,"E0"),sQuery(id+"F0.wireOp",EDGE,"E1"),sQuery(id+"F0.wireOp",EDGE,"E2"),sQuery(id+"F0.wireOp",EDGE,"E3"),sQuery(id+"F0.wireOp",EDGE,"E4"),sQuery(id+"F0.wireOp",EDGE,"E5")])],"isStart":false}),makeQuery(id+"F3.opExtrude","CAP_FACE",FACE,{"disambiguationData":[OSD([sQuery(id+"F2.wireOp",EDGE,"E6.0"),sQuery(id+"F2.wireOp",EDGE,"E6.1"),sQuery(id+"F2.wireOp",EDGE,"E7"),sQuery(id+"F2.wireOp",EDGE,"E8")])],"isStart":true})]}),makeQuery(id+"F17.opExtrude","SWEPT_FACE",FACE,{"disambiguationData":[OSD([sQuery(id+"F16.wireOp",EDGE,"E39.2")])]})]}),"instanceName":"1"}),makeQuery(id+"F35.opExtrude","CAP_FACE",FACE,{"disambiguationData":[OSD([sQuery(id+"F34.wireOp",EDGE,"E64"),sQuery(id+"F34.wireOp",EDGE,"E65")])],"isStart":true})]});
            var sketch = newSketch(context, id + "F38", { "sketchPlane" : qUnion([Q0])});
            skCircle(sketch, "E68", {"center": v(64, 43) * mm, "radius": 2.8 * mm});
            skSolve(sketch);
        }
        {
            var Q0;
            Q0 = qSketchRegion(id + "F38", true);
            extrude(context, id + "F39", {"entities" : qUnion([Q0]), "operationType" : NewBodyOperationType.REMOVE, "oppositeDirection" : true, "depth" : 2 * mm, "offsetDistance" : 25 * mm});
        }
        {
            var Q0;
            Q0=makeQuery(id+"F35.boolean.opBoolean","MERGE",FACE,{"derivedFrom":[makeQuery(id+"F28.opPattern","COPY",FACE,{"derivedFrom":makeQuery(id+"F13.boolean.opBoolean","MERGE",FACE,{"derivedFrom":[makeQuery(id+"F3.opExtrude","CAP_FACE",FACE,{"disambiguationData":[OSD([sQuery(id+"F2.wireOp",EDGE,"E6.0"),sQuery(id+"F2.wireOp",EDGE,"E6.1"),sQuery(id+"F2.wireOp",EDGE,"E7"),sQuery(id+"F2.wireOp",EDGE,"E8")])],"isStart":false})],"fromTools":[makeQuery(id+"F13.opExtrude","SWEPT_FACE",FACE,{"disambiguationData":[OSD([sQuery(id+"F12.wireOp",EDGE,"E34")])]})]}),"instanceName":"1"}),makeQuery(id+"F35.opExtrude","CAP_FACE",FACE,{"disambiguationData":[OSD([sQuery(id+"F34.wireOp",EDGE,"E64"),sQuery(id+"F34.wireOp",EDGE,"E65")])],"isStart":false})]});
            var sketch = newSketch(context, id + "F40", { "sketchPlane" : qUnion([Q0])});
            skCircle(sketch, "E69.cCircle", {"center": v(64, -43) * mm, "radius": 3.12 * mm, "construction": true});
            skLineSegment(sketch, "E69.0", {"start": v(65.56, -45.7) * mm, "end": v(62.44, -45.7) * mm});
            skLineSegment(sketch, "E69.1", {"start": v(62.44, -45.7) * mm, "end": v(60.88, -43) * mm});
            skLineSegment(sketch, "E69.2", {"start": v(60.88, -43) * mm, "end": v(62.44, -40.3) * mm});
            skLineSegment(sketch, "E69.3", {"start": v(62.44, -40.3) * mm, "end": v(65.56, -40.3) * mm});
            skLineSegment(sketch, "E69.4", {"start": v(65.56, -40.3) * mm, "end": v(67.12, -43) * mm});
            skLineSegment(sketch, "E69.5", {"start": v(67.12, -43) * mm, "end": v(65.56, -45.7) * mm});
            skSolve(sketch);
        }
        {
            var Q0;
            Q0 = qSketchRegion(id + "F40", true);
            extrude(context, id + "F41", {"entities" : qUnion([Q0]), "operationType" : NewBodyOperationType.REMOVE, "oppositeDirection" : true, "depth" : 1 * mm, "offsetDistance" : 25 * mm});
        }
        {
            var Q0;
            Q0=makeQuery(id+"F37.boolean.opBoolean","MERGE",FACE,{"derivedFrom":[makeQuery(id+"F28.opPattern","COPY",FACE,{"derivedFrom":makeQuery(id+"F13.boolean.opBoolean","MERGE",FACE,{"derivedFrom":[makeQuery(id+"F10.opExtrude","CAP_FACE",FACE,{"disambiguationData":[OSD([sQuery(id+"F9.wireOp",EDGE,"E21.0.0"),sQuery(id+"F9.wireOp",EDGE,"E21.0.1"),sQuery(id+"F9.wireOp",EDGE,"E21.0.2"),sQuery(id+"F9.wireOp",EDGE,"E21.0.3"),sQuery(id+"F9.wireOp",EDGE,"E21.0.4")])],"isStart":true})],"fromTools":[makeQuery(id+"F13.opExtrude","SWEPT_FACE",FACE,{"disambiguationData":[OSD([sQuery(id+"F12.wireOp",EDGE,"E24.top")])]})]}),"instanceName":"1"}),makeQuery(id+"F37.opExtrude","CAP_FACE",FACE,{"disambiguationData":[OSD([sQuery(id+"F36.wireOp",EDGE,"E66"),sQuery(id+"F36.wireOp",EDGE,"E67")])],"isStart":false})]});
            var sketch = newSketch(context, id + "F42", { "sketchPlane" : qUnion([Q0])});
            skCircle(sketch, "E70", {"center": v(64, 43) * mm, "radius": 3.4 * mm});
            skSolve(sketch);
        }
        {
            var Q0;
            Q0 = qSketchRegion(id + "F42", true);
            extrude(context, id + "F43", {"entities" : qUnion([Q0]), "operationType" : NewBodyOperationType.REMOVE, "oppositeDirection" : true, "depth" : 0.4 * mm, "offsetDistance" : 25 * mm});
        }
        {
            var Q0;
            Q0=makeQuery(id+"F31.boolean.opBoolean","MERGE",FACE,{"derivedFrom":[makeQuery(id+"F28.opPattern","COPY",FACE,{"derivedFrom":makeQuery(id+"F19.opExtrude","CAP_FACE",FACE,{"disambiguationData":[OSD([sQuery(id+"F18.wireOp",EDGE,"E40"),sQuery(id+"F18.wireOp",EDGE,"E41"),sQuery(id+"F18.wireOp",EDGE,"E42"),sQuery(id+"F18.wireOp",EDGE,"E43"),sQuery(id+"F18.wireOp",EDGE,"E44"),sQuery(id+"F18.wireOp",EDGE,"E45"),sQuery(id+"F18.wireOp",EDGE,"E46"),sQuery(id+"F18.wireOp",EDGE,"E47")])],"isStart":false}),"instanceName":"1"}),makeQuery(id+"F31.opExtrude","CAP_FACE",FACE,{"disambiguationData":[OSD([sQuery(id+"F30.wireOp",EDGE,"E55")])],"isStart":false}),makeQuery(id+"F31.opExtrude","CAP_FACE",FACE,{"disambiguationData":[OSD([sQuery(id+"F30.wireOp",EDGE,"E56")])],"isStart":false}),makeQuery(id+"F31.opExtrude","CAP_FACE",FACE,{"disambiguationData":[OSD([sQuery(id+"F30.wireOp",EDGE,"E57")])],"isStart":false}),makeQuery(id+"F31.opExtrude","CAP_FACE",FACE,{"disambiguationData":[OSD([sQuery(id+"F30.wireOp",EDGE,"E58")])],"isStart":false})]});
            extrude(context, id + "F44", {"entities" : qUnion([Q0]), "operationType" : NewBodyOperationType.ADD, "depth" : 2 * mm, "offsetDistance" : 25 * mm});
        }
    });
